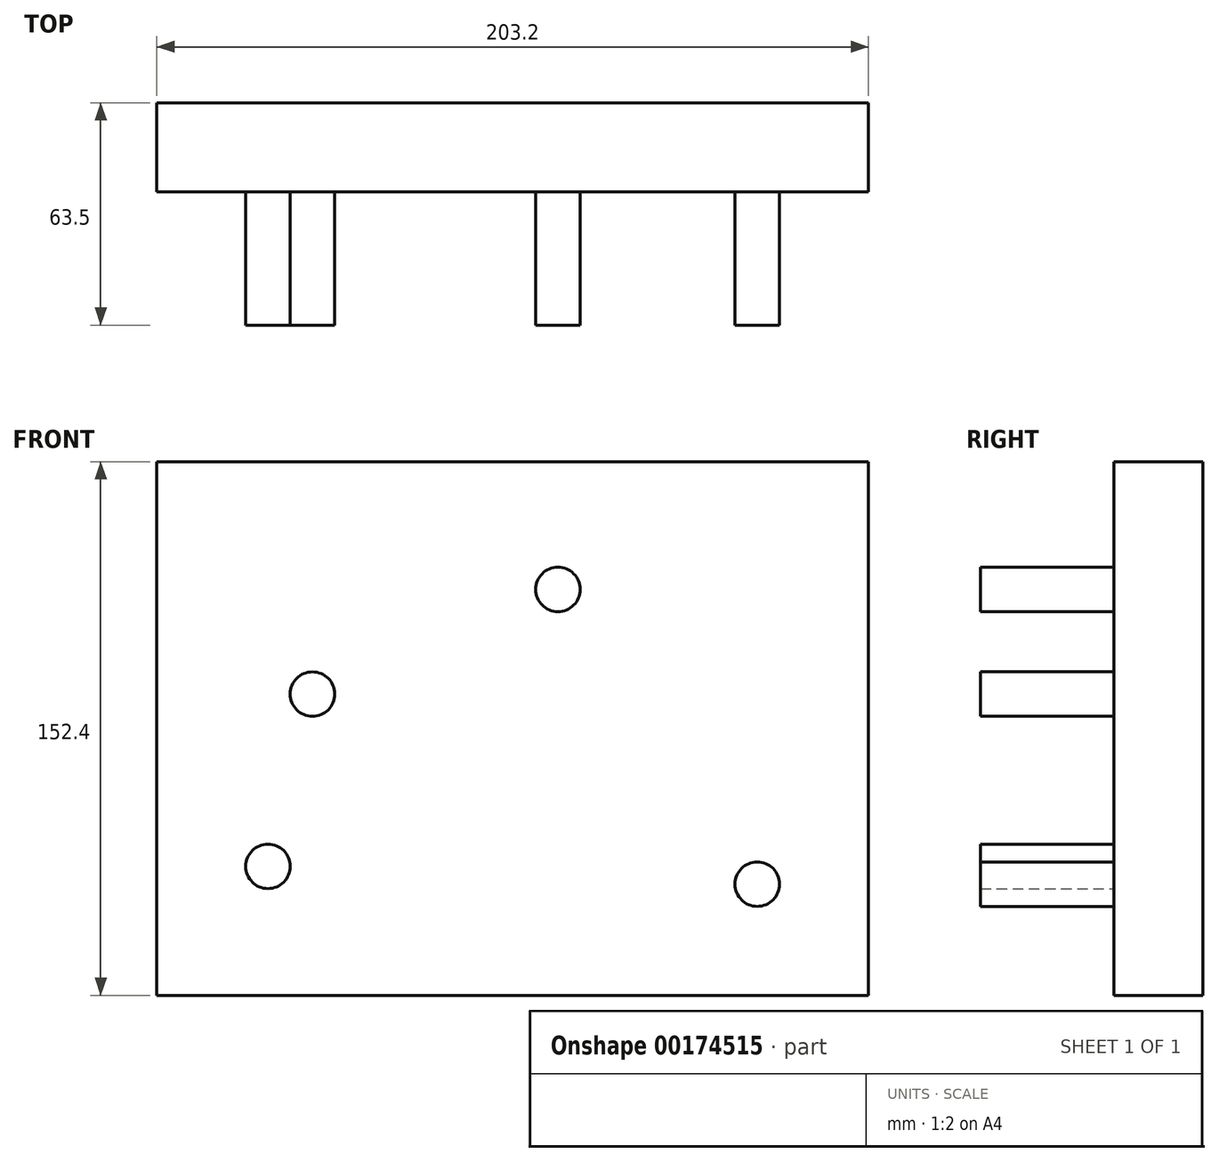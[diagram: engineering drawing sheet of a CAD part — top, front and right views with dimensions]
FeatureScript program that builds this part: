
annotation { "Feature Type Name" : "Feature", "Feature Type Description" : "" }
export const myFeature = defineFeature(function(context is Context, id is Id, definition is map)
    precondition{}
    {
        {
            var Q0;
            Q0=qCreatedBy(makeId("Front.planeOp"),FACE);
            var sketch = newSketch(context, id + "F0", { "sketchPlane" : qUnion([Q0])});
            skLineSegment(sketch, "E0.bottom", {"start": v(-101.6, 76.2) * mm, "end": v(101.6, 76.2) * mm});
            skLineSegment(sketch, "E0.top", {"start": v(-101.6, -76.2) * mm, "end": v(101.6, -76.2) * mm});
            skLineSegment(sketch, "E0.left", {"start": v(-101.6, 76.2) * mm, "end": v(-101.6, -76.2) * mm});
            skLineSegment(sketch, "E0.right", {"start": v(101.6, 76.2) * mm, "end": v(101.6, -76.2) * mm});
            skSolve(sketch);
        }
        {
            var Q0;
            Q0=makeQuery(id+"F0.imprint","IMPRINT",FACE,{"disambiguationData":[TD([[makeQuery(id+"F0.imprint","IMPRINT",EDGE,{"derivedFrom":sQuery(id+"F0.wireOp",EDGE,"E0.bottom")}),-1.0]])]});
            extrude(context, id + "F1", {"entities" : qUnion([Q0]), "depth" : 25.4 * mm});
        }
        {
            var Q0;
            Q0=makeQuery(id+"F1.opExtrude","CAP_FACE",FACE,{"disambiguationData":[OSD([sQuery(id+"F0.wireOp",EDGE,"E0.bottom"),sQuery(id+"F0.wireOp",EDGE,"E0.top"),sQuery(id+"F0.wireOp",EDGE,"E0.left"),sQuery(id+"F0.wireOp",EDGE,"E0.right")])],"isStart":false});
            var sketch = newSketch(context, id + "F2", { "sketchPlane" : qUnion([Q0])});
            skCircle(sketch, "E1", {"center": v(-57.15, 9.82) * mm, "radius": 6.35 * mm});
            skCircle(sketch, "E2", {"center": v(-69.85, -39.37) * mm, "radius": 6.35 * mm});
            skCircle(sketch, "E3", {"center": v(12.94, 39.72) * mm, "radius": 6.35 * mm});
            skCircle(sketch, "E4", {"center": v(69.85, -44.45) * mm, "radius": 6.35 * mm});
            skSolve(sketch);
        }
        {
            var Q0;
            Q0=makeQuery(id+"F2.imprint","IMPRINT",FACE,{"disambiguationData":[TD([[makeQuery(id+"F2.imprint","IMPRINT",EDGE,{"derivedFrom":sQuery(id+"F2.wireOp",EDGE,"E3")}),1.0]])]});
            var Q1;
            Q1=makeQuery(id+"F2.imprint","IMPRINT",FACE,{"disambiguationData":[TD([[makeQuery(id+"F2.imprint","IMPRINT",EDGE,{"derivedFrom":sQuery(id+"F2.wireOp",EDGE,"E1")}),1.0]])]});
            var Q2;
            Q2=makeQuery(id+"F2.imprint","IMPRINT",FACE,{"disambiguationData":[TD([[makeQuery(id+"F2.imprint","IMPRINT",EDGE,{"derivedFrom":sQuery(id+"F2.wireOp",EDGE,"E2")}),1.0]])]});
            var Q3;
            Q3=makeQuery(id+"F2.imprint","IMPRINT",FACE,{"disambiguationData":[TD([[makeQuery(id+"F2.imprint","IMPRINT",EDGE,{"derivedFrom":sQuery(id+"F2.wireOp",EDGE,"E4")}),1.0]])]});
            extrude(context, id + "F3", {"entities" : qUnion([Q0, Q1, Q2, Q3]), "operationType" : NewBodyOperationType.ADD, "depth" : 38.1 * mm});
        }
    });
